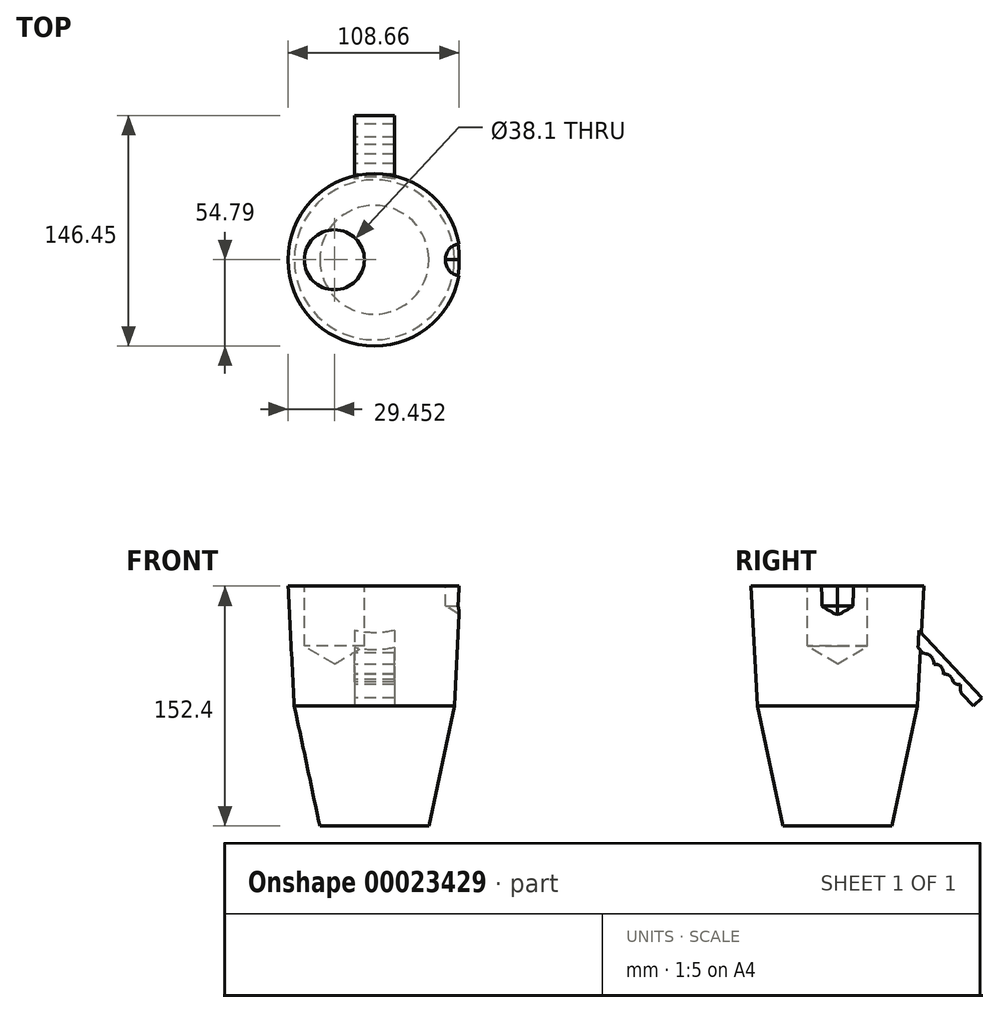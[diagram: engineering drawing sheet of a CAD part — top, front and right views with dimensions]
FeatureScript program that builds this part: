
annotation { "Feature Type Name" : "Feature", "Feature Type Description" : "" }
export const myFeature = defineFeature(function(context is Context, id is Id, definition is map)
    precondition{}
    {
        {
            var Q0;
            Q0=qCreatedBy(makeId("Top.planeOp"),FACE);
            var sketch = newSketch(context, id + "F0", { "sketchPlane" : qUnion([Q0])});
            skCircle(sketch, "E0", {"center": v(0, 0) * mm, "radius": 50.8 * mm});
            skCircle(sketch, "E1", {"center": v(0, 0) * mm, "radius": 47.63 * mm});
            skSolve(sketch);
        }
        {
            var Q0;
            Q0=makeQuery(id+"F0.imprint","IMPRINT",FACE,{"disambiguationData":[TD([[makeQuery(id+"F0.imprint","IMPRINT",EDGE,{"derivedFrom":sQuery(id+"F0.wireOp",EDGE,"E0")}),1.0]])]});
            var Q1;
            Q1=makeQuery(id+"F0.imprint","IMPRINT",FACE,{"disambiguationData":[TD([[makeQuery(id+"F0.imprint","IMPRINT",EDGE,{"derivedFrom":sQuery(id+"F0.wireOp",EDGE,"E1")}),1.0]])]});
            extrude(context, id + "F1", {"entities" : qUnion([Q0, Q1]), "oppositeDirection" : true, "depth" : 76.2 * mm, "hasDraft" : true, "draftAngle" : 12 * degree, "draftPullDirection" : true, "hasSecondDirection" : true, "secondDirectionOppositeDirection" : false, "secondDirectionDepth" : 76.2 * mm, "hasSecondDirectionDraft" : true, "secondDirectionDraftAngle" : 3 * degree});
        }
        {
            var Q0;
            Q0=makeQuery(id+"F1.opExtrude","CAP_FACE",FACE,{"disambiguationData":[OSD([sQuery(id+"F0.wireOp",EDGE,"E0")])],"isStart":true});
            var sketch = newSketch(context, id + "F2", { "sketchPlane" : qUnion([Q0])});
            skLineSegment(sketch, "E2", {"start": v(-25.34, -2.54) * mm, "end": v(-25.34, 0) * mm});
            skLineSegment(sketch, "E3", {"start": v(-25.34, -48.58) * mm, "end": v(-25.34, 48.58) * mm, "construction": true});
            skArc(sketch, "E4", {"start": v(-25.34, 0) * mm, "mid": v(-25.37, -1.27) * mm, "end": v(-25.34, -2.54) * mm});
            skSolve(sketch);
        }
        {
            var Q0;
            Q0=makeQuery(id+"F1.opExtrude","CAP_FACE",FACE,{"disambiguationData":[OSD([sQuery(id+"F0.wireOp",EDGE,"E0")])],"isStart":true});
            var sketch = newSketch(context, id + "F3", { "sketchPlane" : qUnion([Q0])});
            skLineSegment(sketch, "E5", {"start": v(54.8, -0.55) * mm, "end": v(54.8, 0.55) * mm, "construction": true});
            skSolve(sketch);
        }
        {
            var Q0;
            Q0=sQuery(id+"F3.wireOp",VERTEX,"E5.start");
            var Q1;
            Q1=sQuery(id+"F3.wireOp",VERTEX,"E5.end");
            var Q2;
            Q2=makeQuery(id+"F1.split0.splitOp","SPLIT",BODY,{"derivedFrom":makeQuery(id+"F1.opExtrude","SWEPT_BODY",BODY,{"disambiguationData":[OSD([sQuery(id+"F0.wireOp",EDGE,"E0")])]})});
            hole(context, id + "F4", {"style" : HoleStyle.SIMPLE, "holeDiameter" : 19.05 * mm, "endStyle" : HoleEndStyle.BLIND, "holeDepth" : 12.7 * mm, "locations" : qUnion([Q0, Q1]), "scope" : qUnion([Q2])});
        }
        {
            var Q0;
            Q0=sQuery(id+"F2.wireOp",VERTEX,"E4.start");
            var Q1;
            Q1=makeQuery(id+"F1.split0.splitOp","SPLIT",BODY,{"derivedFrom":makeQuery(id+"F1.opExtrude","SWEPT_BODY",BODY,{"disambiguationData":[OSD([sQuery(id+"F0.wireOp",EDGE,"E0")])]})});
            hole(context, id + "F5", {"style" : HoleStyle.SIMPLE, "holeDiameter" : 38.1 * mm, "endStyle" : HoleEndStyle.BLIND, "holeDepth" : 38.1 * mm, "locations" : qUnion([Q0]), "scope" : qUnion([Q1])});
        }
        {
            var Q0;
            Q0=qCreatedBy(makeId("Right.planeOp"),FACE);
            var sketch = newSketch(context, id + "F6", { "sketchPlane" : qUnion([Q0])});
            skLineSegment(sketch, "E6", {"start": v(38.27, 50.83) * mm, "end": v(54.36, 33.81) * mm});
            skLineSegment(sketch, "E7", {"start": v(44.62, 55.85) * mm, "end": v(91.66, 5.13) * mm});
            skLineSegment(sketch, "E8", {"start": v(54.36, 33.81) * mm, "end": v(56.48, 33.26) * mm});
            skLineSegment(sketch, "E9", {"start": v(61.22, 27.12) * mm, "end": v(61.22, 26.56) * mm});
            skLineSegment(sketch, "E10", {"start": v(61.22, 26.56) * mm, "end": v(62.1, 26.56) * mm});
            skLineSegment(sketch, "E11", {"start": v(67.18, 21.48) * mm, "end": v(67.18, 20.26) * mm});
            skLineSegment(sketch, "E12", {"start": v(73.26, 15.22) * mm, "end": v(73.26, 17.04) * mm});
            skLineSegment(sketch, "E13", {"start": v(67.99, 20.3) * mm, "end": v(67.18, 20.26) * mm});
            skLineSegment(sketch, "E14", {"start": v(76.46, 13.84) * mm, "end": v(78.08, 13.84) * mm});
            skLineSegment(sketch, "E15", {"start": v(78.08, 13.84) * mm, "end": v(78.08, 10.76) * mm});
            skLineSegment(sketch, "E16", {"start": v(79.47, 7.27) * mm, "end": v(86.34, 0) * mm});
            skLineSegment(sketch, "E17", {"start": v(91.66, 5.13) * mm, "end": v(86.34, 0) * mm});
            skLineSegment(sketch, "E18", {"start": v(44.62, 55.85) * mm, "end": v(38.27, 50.83) * mm});
            skPoint(sketch, "E19.visualSharp", {"position": v(61.22, 32.02) * mm});
            skArc(sketch, "E19.filletArc", {"start": v(61.22, 27.12) * mm, "mid": v(59.9, 31) * mm, "end": v(56.48, 33.26) * mm});
            skPoint(sketch, "E20.visualSharp", {"position": v(78.08, 8.74) * mm});
            skArc(sketch, "E20.filletArc", {"start": v(78.08, 10.76) * mm, "mid": v(78.44, 8.88) * mm, "end": v(79.47, 7.27) * mm});
            skLineSegment(sketch, "E21.trimOffspring", {"start": v(78.08, 8.74) * mm, "end": v(86.34, 0) * mm});
            skPoint(sketch, "E22.visualSharp", {"position": v(67.18, 26.56) * mm});
            skArc(sketch, "E22.filletArc", {"start": v(67.18, 21.48) * mm, "mid": v(65.69, 25.07) * mm, "end": v(62.1, 26.56) * mm});
            skPoint(sketch, "E23.visualSharp", {"position": v(73.26, 13.84) * mm});
            skArc(sketch, "E23.filletArc", {"start": v(73.26, 17.04) * mm, "mid": v(74.2, 14.77) * mm, "end": v(76.46, 13.84) * mm});
            skPoint(sketch, "E24.visualSharp", {"position": v(73.26, 20.49) * mm});
            skArc(sketch, "E24.filletArc", {"start": v(73.26, 15.22) * mm, "mid": v(71.7, 18.87) * mm, "end": v(67.99, 20.3) * mm});
            skSolve(sketch);
        }
        {
            var Q0;
            Q0 = qSketchRegion(id + "F6", true);
            extrude(context, id + "F7", {"entities" : qUnion([Q0]), "operationType" : NewBodyOperationType.ADD, "depth" : 12.7 * mm, "hasSecondDirection" : true, "secondDirectionOppositeDirection" : true, "secondDirectionDepth" : 12.7 * mm});
        }
    });
